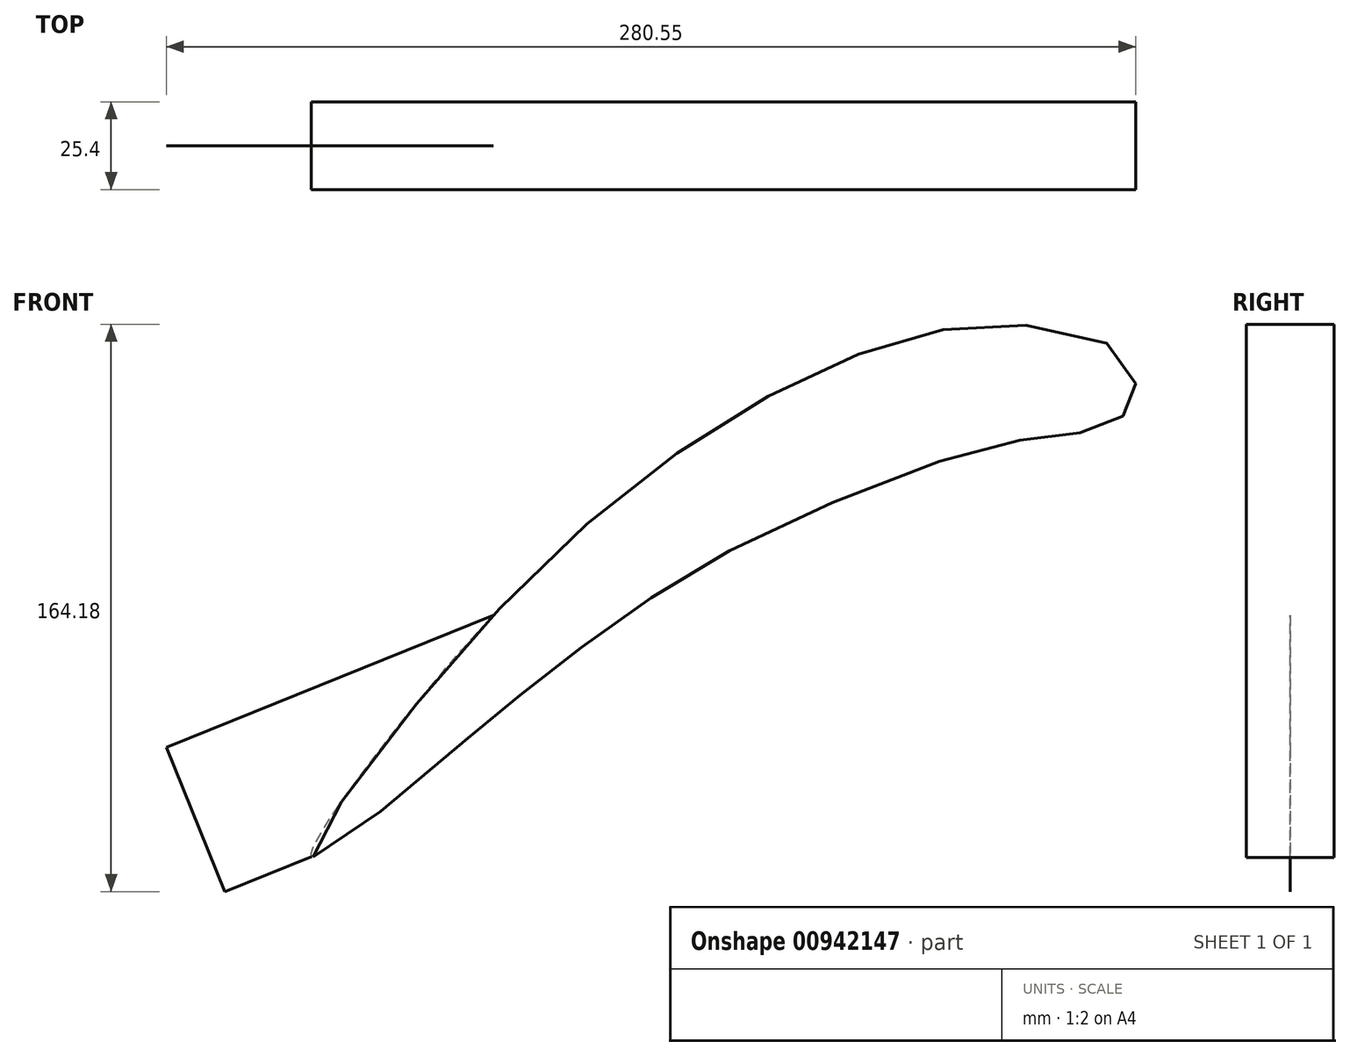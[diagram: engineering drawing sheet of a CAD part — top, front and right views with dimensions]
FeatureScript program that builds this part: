
annotation { "Feature Type Name" : "Feature", "Feature Type Description" : "" }
export const myFeature = defineFeature(function(context is Context, id is Id, definition is map)
    precondition{}
    {
        {
            var Q0;
            Q0=qCreatedBy(makeId("Front.planeOp"),FACE);
            var sketch = newSketch(context, id + "F0", { "sketchPlane" : qUnion([Q0])});
            skFitSpline(sketch, "E0", {"points": [v(0, 0) * mm, v(17, 28) * mm, v(71, 89) * mm, v(124, 129) * mm, v(170, 149.81) * mm, v(206, 154) * mm, v(235, 145.17) * mm, v(238, 135) * mm, v(236, 129.5) * mm, v(229, 124.5) * mm, v(214, 122) * mm, v(187, 116.4) * mm, v(125, 91) * mm, v(88.5, 68.64) * mm, v(61, 47.81) * mm, v(40, 30.5) * mm, v(0, 0) * mm]});
            skLineSegment(sketch, "E1", {"start": v(0, 0) * mm, "end": v(238, 135) * mm, "construction": true});
            skSolve(sketch);
        }
        {
            var Q0;
            Q0=qSketchRegion(id+"F0",true);
            extrude(context, id + "F1", {"entities" : qUnion([Q0]), "depth" : 12.7 * mm, "offsetDistance" : 25.4 * mm, "hasSecondDirection" : true, "secondDirectionOppositeDirection" : true, "secondDirectionDepth" : 12.7 * mm});
        }
        {
            var Q0;
            Q0=qCreatedBy(makeId("Front.planeOp"),FACE);
            var sketch = newSketch(context, id + "F2", { "sketchPlane" : qUnion([Q0])});
            skLineSegment(sketch, "E2", {"start": v(52.12, 70) * mm, "end": v(-42.46, 31.8) * mm});
            skLineSegment(sketch, "E3", {"start": v(-42.46, 31.8) * mm, "end": v(-25.6, -9.93) * mm});
            skLineSegment(sketch, "E4", {"start": v(-42.46, 31.8) * mm, "end": v(6.84, 31.8) * mm, "construction": true});
            skLineSegment(sketch, "E5", {"start": v(-25.6, -9.93) * mm, "end": v(-0.41, 0.24) * mm});
            skLineSegment(sketch, "E6", {"start": v(-0.41, 0.24) * mm, "end": v(55.18, 67.9) * mm});
            skLineSegment(sketch, "E7", {"start": v(55.18, 67.9) * mm, "end": v(52.12, 70) * mm});
            skSolve(sketch);
        }
        {
            var Q0;
            Q0 = qSketchRegion(id + "F2", true);
            extrude(context, id + "F3", {"entities" : qUnion([Q0]), "operationType" : NewBodyOperationType.ADD, "endBound" : BoundingType.SYMMETRIC, "depth" : 1 / 406.4 * mm, "offsetDistance" : 25 * mm});
        }
    });
